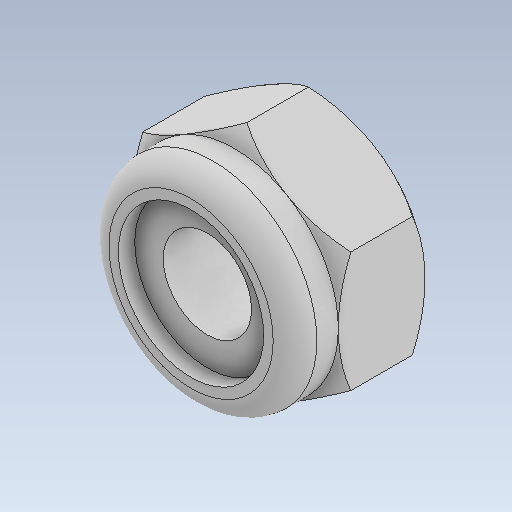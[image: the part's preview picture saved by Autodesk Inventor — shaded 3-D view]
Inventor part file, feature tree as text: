
AUTODESK INVENTOR PART (.ipt)
format: ipt  version: 2020.2 (Build 242310000, 310)  size: 162,304 bytes
history: native  units: in
note: dims shown in document units (in); Inventor stores cm internally (conversion verified against a paired STEP export)
features: fillet x1
ambient origin geometry x8: Origin, YZ Plane, XZ Plane, XY Plane, X Axis, Y Axis, Z Axis, Center Point
bodies: Solid1 (feature_tree)
feature tree (1):
  fillet  "Fillet1"  [1 undecoded]
note: 1 required parameter value undecoded (feature->parameter linkage not recoverable at this tier; creation-order binding heuristic only, values carry confidence <= 0.55)
